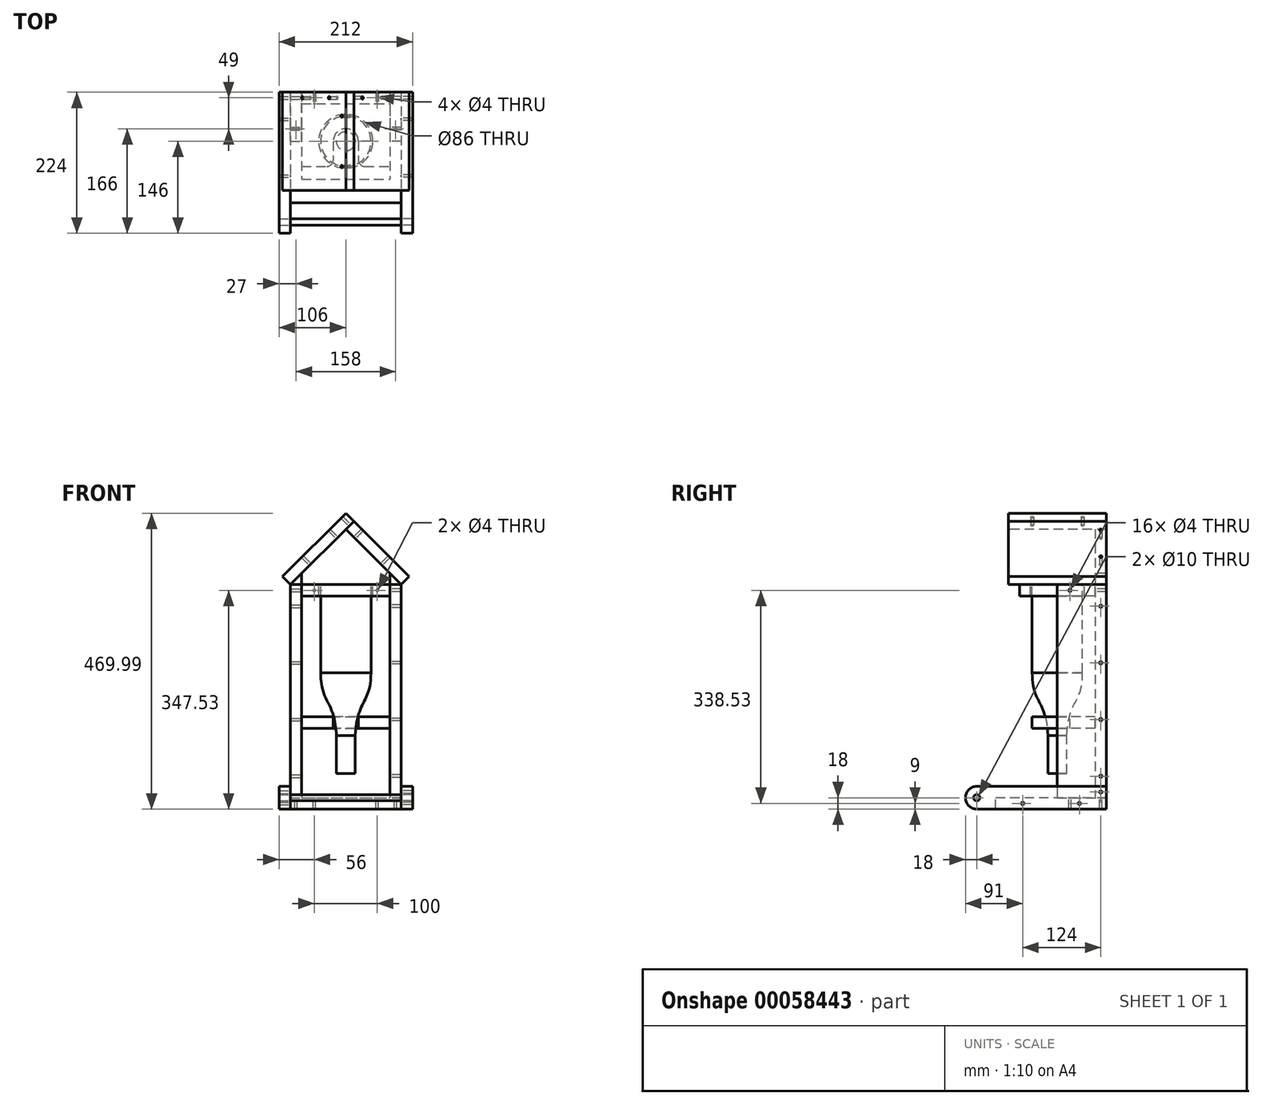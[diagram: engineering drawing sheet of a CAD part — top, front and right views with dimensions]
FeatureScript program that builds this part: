
annotation { "Feature Type Name" : "Feature", "Feature Type Description" : "" }
export const myFeature = defineFeature(function(context is Context, id is Id, definition is map)
    precondition{}
    {
        {
            assignVariable(context, id + "F0", {"name" : "Thickness", "anyValue" : 18});
        }
        {
            var Q0;
            Q0=qCreatedBy(makeId("Front.planeOp"),FACE);
            var sketch = newSketch(context, id + "F1", { "sketchPlane" : qUnion([Q0])});
            skLineSegment(sketch, "E0", {"start": v(0, 0) * mm, "end": v(40, 0) * mm});
            skLineSegment(sketch, "E1", {"start": v(40, 0) * mm, "end": v(40, -140) * mm});
            skLineSegment(sketch, "E2", {"start": v(15, -240) * mm, "end": v(15, -300) * mm});
            skLineSegment(sketch, "E3", {"start": v(0, 0) * mm, "end": v(0, -300) * mm});
            skLineSegment(sketch, "E4", {"start": v(15, -300) * mm, "end": v(0, -300) * mm});
            skFitSpline(sketch, "E5", {"points": [v(40, -140) * mm, v(15, -240) * mm], "startDerivative": vector(-0.64, -151.3) * mm, "endDerivative": vector(-7.4, -174.03) * mm});
            skSolve(sketch);
        }
        {
            var Q0;
            Q0=makeQuery(id+"F1.imprint","IMPRINT",FACE,{"disambiguationData":[TD([[makeQuery(id+"F1.imprint","IMPRINT",EDGE,{"derivedFrom":sQuery(id+"F1.wireOp",EDGE,"E0")}),-1.0]])]});
            var Q1;
            Q1=sQuery(id+"F1.wireOp",EDGE,"E3");
            revolve(context, id + "F2", {"entities" : qUnion([Q0]), "axis" : qUnion([Q1]), "revolveType" : RevolveType.FULL});
        }
        {
            var Q0;
            Q0=qCreatedBy(makeId("Front.planeOp"),FACE);
            cPlane(context, id + "F3", {"entities" : qUnion([Q0]), "cplaneType" : CPlaneType.OFFSET, "offset" : 60 * mm, "oppositeDirection" : true, "width" : 150 * mm, "height" : 150 * mm});
        }
        {
            var Q0;
            Q0=qCreatedBy(id+"F3.planeOp",FACE);
            var sketch = newSketch(context, id + "F4", { "sketchPlane" : qUnion([Q0])});
            skLineSegment(sketch, "E6.bottom", {"start": v(-70, 18) * mm, "end": v(70, 18) * mm, "construction": true});
            skLineSegment(sketch, "E6.top", {"start": v(-70, -338.53) * mm, "end": v(70, -338.53) * mm});
            skLineSegment(sketch, "E6.left", {"start": v(-70, 18) * mm, "end": v(-70, -338.53) * mm});
            skLineSegment(sketch, "E6.right", {"start": v(70, 18) * mm, "end": v(70, -338.53) * mm});
            skLineSegment(sketch, "E7.bottom", {"start": v(70, 0) * mm, "end": v(88, 0) * mm, "construction": true});
            skLineSegment(sketch, "E7.top", {"start": v(70, -338.53) * mm, "end": v(88, -338.53) * mm, "construction": true});
            skLineSegment(sketch, "E7.left", {"start": v(70, 0) * mm, "end": v(70, -338.53) * mm});
            skLineSegment(sketch, "E7.right", {"start": v(88, 0) * mm, "end": v(88, -338.53) * mm, "construction": true});
            skLineSegment(sketch, "E8", {"start": v(-40, -140) * mm, "end": v(-40, 0) * mm, "construction": true});
            skLineSegment(sketch, "E9", {"start": v(0, 18) * mm, "end": v(0, -338.53) * mm, "construction": true});
            skLineSegment(sketch, "E10.MirrorCS", {"start": v(-70, -338.53) * mm, "end": v(-88, -338.53) * mm, "construction": true});
            skLineSegment(sketch, "E11.MirrorCS", {"start": v(-88, 0) * mm, "end": v(-88, -338.53) * mm, "construction": true});
            skLineSegment(sketch, "E12.MirrorCS", {"start": v(-70, 0) * mm, "end": v(-88, 0) * mm, "construction": true});
            skLineSegment(sketch, "E13", {"start": v(-70, 18) * mm, "end": v(0, 88) * mm});
            skLineSegment(sketch, "E14", {"start": v(0, 88) * mm, "end": v(70, 18) * mm});
            skLineSegment(sketch, "E15", {"start": v(70, -9) * mm, "end": v(-70, -9) * mm, "construction": true});
            skCircle(sketch, "E16", {"center": v(50, -9) * mm, "radius": 2 * mm});
            skCircle(sketch, "E17.MirrorC", {"center": v(-50, -9) * mm, "radius": 2 * mm});
            skSolve(sketch);
        }
        {
            var Q0;
            Q0 = qSketchRegion(id + "F4", true);
            extrude(context, id + "F5", {"entities" : qUnion([Q0]), "oppositeDirection" : true, "depth" : (getVariable(context, 'Thickness')) * mm});
        }
        {
            var Q0;
            Q0=makeQuery(id+"F5.opExtrude","SWEPT_FACE",FACE,{"disambiguationData":[OSD([sQuery(id+"F4.wireOp",EDGE,"E6.right"),sQuery(id+"F4.wireOp",EDGE,"E7.left")])]});
            var sketch = newSketch(context, id + "F6", { "sketchPlane" : qUnion([Q0])});
            skLineSegment(sketch, "E18.bottom", {"start": v(78, 0) * mm, "end": v(0, 0) * mm});
            skLineSegment(sketch, "E18.top", {"start": v(78, -338.53) * mm, "end": v(0, -338.53) * mm});
            skLineSegment(sketch, "E18.left", {"start": v(78, 0) * mm, "end": v(78, -338.53) * mm});
            skLineSegment(sketch, "E18.right", {"start": v(0, 0) * mm, "end": v(0, -338.53) * mm});
            skLineSegment(sketch, "E19", {"start": v(69, 0) * mm, "end": v(69, -338.53) * mm, "construction": true});
            skCircle(sketch, "E20", {"center": v(69, -34.26) * mm, "radius": 2 * mm});
            skCircle(sketch, "E21.0.1.0", {"center": v(69, -124.26) * mm, "radius": 2 * mm});
            skCircle(sketch, "E21.0.2.0", {"center": v(69, -214.26) * mm, "radius": 2 * mm});
            skCircle(sketch, "E21.0.3.0", {"center": v(69, -304.26) * mm, "radius": 2 * mm});
            skLineSegment(sketch, "E21.direction1", {"start": v(69, -34.26) * mm, "end": v(84, -34.26) * mm, "construction": true});
            skLineSegment(sketch, "E21.direction2", {"start": v(69, -34.26) * mm, "end": v(69, -124.26) * mm, "construction": true});
            skLineSegment(sketch, "E22", {"start": v(60, -169.26) * mm, "end": v(78, -169.26) * mm, "construction": true});
            skLineSegment(sketch, "E23", {"start": v(78, -9) * mm, "end": v(0, -9) * mm, "construction": true});
            skCircle(sketch, "E24", {"center": v(20, -9) * mm, "radius": 2 * mm});
            skSolve(sketch);
        }
        {
            var Q0;
            Q0 = qSketchRegion(id + "F6", true);
            extrude(context, id + "F7", {"entities" : qUnion([Q0]), "depth" : (getVariable(context, 'Thickness')) * mm});
        }
        {
            var Q0;
            Q0=makeQuery(id+"F5.opExtrude","SWEPT_FACE",FACE,{"disambiguationData":[OSD([sQuery(id+"F4.wireOp",EDGE,"E6.left")])]});
            var sketch = newSketch(context, id + "F8", { "sketchPlane" : qUnion([Q0])});
            skLineSegment(sketch, "E25.bottom", {"start": v(0, 0) * mm, "end": v(-78, 0) * mm});
            skLineSegment(sketch, "E25.top", {"start": v(0, -338.53) * mm, "end": v(-78, -338.53) * mm});
            skLineSegment(sketch, "E25.left", {"start": v(0, 0) * mm, "end": v(0, -338.53) * mm});
            skLineSegment(sketch, "E25.right", {"start": v(-78, 0) * mm, "end": v(-78, -338.53) * mm});
            skCircle(sketch, "E26.0", {"center": v(-69, -34.26) * mm, "radius": 2 * mm});
            skCircle(sketch, "E27.0", {"center": v(-69, -124.26) * mm, "radius": 2 * mm});
            skCircle(sketch, "E28.0", {"center": v(-69, -214.26) * mm, "radius": 2 * mm});
            skCircle(sketch, "E29.0", {"center": v(-69, -304.26) * mm, "radius": 2 * mm});
            skCircle(sketch, "E30.0", {"center": v(-20, -9) * mm, "radius": 2 * mm});
            skSolve(sketch);
        }
        {
            var Q0;
            Q0 = qSketchRegion(id + "F8", true);
            extrude(context, id + "F9", {"entities" : qUnion([Q0]), "depth" : (getVariable(context, 'Thickness')) * mm});
        }
        {
            var Q0;
            Q0=makeQuery(id+"F5.opExtrude","SWEPT_FACE",FACE,{"disambiguationData":[OSD([sQuery(id+"F4.wireOp",EDGE,"E14")])]});
            var sketch = newSketch(context, id + "F10", { "sketchPlane" : qUnion([Q0])});
            skLineSegment(sketch, "E31.bottom", {"start": v(78, 62.23) * mm, "end": v(-78, 62.23) * mm});
            skLineSegment(sketch, "E31.top", {"start": v(78, -62.23) * mm, "end": v(-78, -62.23) * mm});
            skLineSegment(sketch, "E31.left", {"start": v(78, 62.23) * mm, "end": v(78, -62.23) * mm});
            skLineSegment(sketch, "E31.right", {"start": v(-78, 62.23) * mm, "end": v(-78, -62.23) * mm});
            skLineSegment(sketch, "E32", {"start": v(69, 62.23) * mm, "end": v(69, -36.77) * mm, "construction": true});
            skCircle(sketch, "E33", {"center": v(69, 42.73) * mm, "radius": 2 * mm});
            skCircle(sketch, "E34", {"center": v(69, -17.27) * mm, "radius": 2 * mm});
            skLineSegment(sketch, "E35", {"start": v(60, 12.73) * mm, "end": v(78, 12.73) * mm, "construction": true});
            skSolve(sketch);
        }
        {
            var Q0;
            Q0 = qSketchRegion(id + "F10", true);
            extrude(context, id + "F11", {"entities" : qUnion([Q0]), "depth" : (getVariable(context, 'Thickness')) * mm});
        }
        {
            var Q0;
            Q0=makeQuery(id+"F5.opExtrude","SWEPT_FACE",FACE,{"disambiguationData":[OSD([sQuery(id+"F4.wireOp",EDGE,"E13")])]});
            var sketch = newSketch(context, id + "F12", { "sketchPlane" : qUnion([Q0])});
            skLineSegment(sketch, "E36.bottom", {"start": v(78, 80.23) * mm, "end": v(-78, 80.23) * mm});
            skLineSegment(sketch, "E36.top", {"start": v(78, -62.23) * mm, "end": v(-78, -62.23) * mm});
            skLineSegment(sketch, "E36.left", {"start": v(78, 80.23) * mm, "end": v(78, -62.23) * mm});
            skLineSegment(sketch, "E36.right", {"start": v(-78, 80.23) * mm, "end": v(-78, -62.23) * mm});
            skLineSegment(sketch, "E37", {"start": v(-69, 62.23) * mm, "end": v(-69, -36.77) * mm, "construction": true});
            skCircle(sketch, "E38", {"center": v(-69, 42.73) * mm, "radius": 2 * mm});
            skCircle(sketch, "E39", {"center": v(-69, -17.27) * mm, "radius": 2 * mm});
            skLineSegment(sketch, "E40", {"start": v(-78, 12.73) * mm, "end": v(-60, 12.73) * mm, "construction": true});
            skLineSegment(sketch, "E41", {"start": v(-78, 71.23) * mm, "end": v(78, 71.23) * mm, "construction": true});
            skCircle(sketch, "E42", {"center": v(-40, 71.23) * mm, "radius": 2 * mm});
            skCircle(sketch, "E43", {"center": v(40, 71.23) * mm, "radius": 2 * mm});
            skLineSegment(sketch, "E44", {"start": v(0, 80.23) * mm, "end": v(0, 62.23) * mm, "construction": true});
            skPoint(sketch, "E44.endSnap0", {"position": v(0, 71.23) * mm});
            skSolve(sketch);
        }
        {
            var Q0;
            Q0 = qSketchRegion(id + "F12", true);
            extrude(context, id + "F13", {"entities" : qUnion([Q0]), "depth" : (getVariable(context, 'Thickness')) * mm});
        }
        {
            var Q0;
            Q0=makeQuery(id+"F7.opExtrude","SWEPT_FACE",FACE,{"disambiguationData":[OSD([sQuery(id+"F6.wireOp",EDGE,"E18.bottom")])]});
            var sketch = newSketch(context, id + "F14", { "sketchPlane" : qUnion([Q0])});
            skLineSegment(sketch, "E45.bottom", {"start": v(-70, 60) * mm, "end": v(70, 60) * mm});
            skLineSegment(sketch, "E45.top", {"start": v(-70, -60) * mm, "end": v(70, -60) * mm});
            skLineSegment(sketch, "E45.left", {"start": v(-70, 60) * mm, "end": v(-70, -60) * mm});
            skLineSegment(sketch, "E45.right", {"start": v(70, 60) * mm, "end": v(70, -60) * mm});
            skCircle(sketch, "E46.0", {"center": v(0, 0) * mm, "radius": 43 * mm});
            skLineSegment(sketch, "E47", {"start": v(70, 0) * mm, "end": v(-70, 0) * mm, "construction": true});
            skSolve(sketch);
        }
        {
            var Q0;
            Q0 = qSketchRegion(id + "F14", true);
            extrude(context, id + "F15", {"entities" : qUnion([Q0]), "oppositeDirection" : true, "depth" : (getVariable(context, 'Thickness')) * mm});
        }
        {
            var Q0;
            Q0=makeQuery(id+"F15.opExtrude","CAP_FACE",FACE,{"disambiguationData":[OSD([sQuery(id+"F14.wireOp",EDGE,"E45.bottom"),sQuery(id+"F14.wireOp",EDGE,"E45.top"),sQuery(id+"F14.wireOp",EDGE,"E45.left"),sQuery(id+"F14.wireOp",EDGE,"E45.right"),sQuery(id+"F14.wireOp",EDGE,"E46.0")])],"isStart":true});
            cPlane(context, id + "F16", {"entities" : qUnion([Q0]), "cplaneType" : CPlaneType.OFFSET, "offset" : 210 * mm, "oppositeDirection" : true, "width" : 150 * mm, "height" : 150 * mm});
        }
        {
            var Q0;
            Q0=qCreatedBy(id+"F16.planeOp",FACE);
            var sketch = newSketch(context, id + "F17", { "sketchPlane" : qUnion([Q0])});
            skLineSegment(sketch, "E48.bottom", {"start": v(-70, 60) * mm, "end": v(70, 60) * mm});
            skLineSegment(sketch, "E48.top", {"start": v(-70, -40) * mm, "end": v(-30, -40) * mm});
            skLineSegment(sketch, "E48.left", {"start": v(-70, 60) * mm, "end": v(-70, -40) * mm});
            skLineSegment(sketch, "E48.right", {"start": v(70, 60) * mm, "end": v(70, -40) * mm});
            skArc(sketch, "E49.0", {"start": v(20, 0) * mm, "mid": v(0, 20) * mm, "end": v(-20, 0) * mm});
            skLineSegment(sketch, "E50", {"start": v(-20, 0) * mm, "end": v(-20, -30) * mm});
            skLineSegment(sketch, "E51", {"start": v(20, 0) * mm, "end": v(20, -30) * mm});
            skLineSegment(sketch, "E52.trimOffspring", {"start": v(30, -40) * mm, "end": v(70, -40) * mm});
            skPoint(sketch, "E53.visualSharp", {"position": v(-20, -40) * mm});
            skArc(sketch, "E53.filletArc", {"start": v(-30, -40) * mm, "mid": v(-22.93, -37.07) * mm, "end": v(-20, -30) * mm});
            skPoint(sketch, "E54.visualSharp", {"position": v(20, -40) * mm});
            skArc(sketch, "E54.filletArc", {"start": v(20, -30) * mm, "mid": v(22.93, -37.07) * mm, "end": v(30, -40) * mm});
            skSolve(sketch);
        }
        {
            var Q0;
            Q0 = qSketchRegion(id + "F17", true);
            extrude(context, id + "F18", {"entities" : qUnion([Q0]), "oppositeDirection" : true, "depth" : (getVariable(context, 'Thickness')) * mm});
        }
        {
            var Q0;
            Q0=makeQuery(id+"F5.opExtrude","SWEPT_FACE",FACE,{"disambiguationData":[OSD([sQuery(id+"F4.wireOp",EDGE,"E6.top")])]});
            var sketch = newSketch(context, id + "F19", { "sketchPlane" : qUnion([Q0])});
            skLineSegment(sketch, "E55.bottom", {"start": v(-88, -78) * mm, "end": v(88, -78) * mm});
            skLineSegment(sketch, "E55.top", {"start": v(-88, 98) * mm, "end": v(88, 98) * mm});
            skLineSegment(sketch, "E55.left", {"start": v(-88, -78) * mm, "end": v(-88, 98) * mm});
            skLineSegment(sketch, "E55.right", {"start": v(88, -78) * mm, "end": v(88, 98) * mm});
            skLineSegment(sketch, "E56", {"start": v(-79, 0) * mm, "end": v(-79, -78) * mm, "construction": true});
            skLineSegment(sketch, "E57", {"start": v(-88, -69) * mm, "end": v(88, -69) * mm, "construction": true});
            skCircle(sketch, "E58", {"center": v(-79, -20) * mm, "radius": 2 * mm});
            skCircle(sketch, "E59", {"center": v(-50, -69) * mm, "radius": 2 * mm});
            skCircle(sketch, "E60.MirrorC", {"center": v(79, -20) * mm, "radius": 2 * mm});
            skCircle(sketch, "E61.MirrorC", {"center": v(50, -69) * mm, "radius": 2 * mm});
            skSolve(sketch);
        }
        {
            var Q0;
            Q0 = qSketchRegion(id + "F19", true);
            extrude(context, id + "F20", {"entities" : qUnion([Q0]), "depth" : (getVariable(context, 'Thickness')) * mm});
        }
        {
            var Q0;
            Q0=makeQuery(id+"F20.opExtrude","SWEPT_FACE",FACE,{"disambiguationData":[OSD([sQuery(id+"F19.wireOp",EDGE,"E55.left")])]});
            var sketch = newSketch(context, id + "F21", { "sketchPlane" : qUnion([Q0])});
            skLineSegment(sketch, "E62.bottom", {"start": v(-78, -356.53) * mm, "end": v(128, -356.53) * mm});
            skLineSegment(sketch, "E62.top", {"start": v(-78, -320.53) * mm, "end": v(128, -320.53) * mm});
            skLineSegment(sketch, "E62.left", {"start": v(-78, -356.53) * mm, "end": v(-78, -320.53) * mm});
            skLineSegment(sketch, "E63", {"start": v(155.22, -338.53) * mm, "end": v(-78, -338.53) * mm, "construction": true});
            skCircle(sketch, "E64", {"center": v(128, -338.53) * mm, "radius": 5 * mm});
            skArc(sketch, "E65", {"start": v(128, -356.53) * mm, "mid": v(146, -338.53) * mm, "end": v(128, -320.53) * mm});
            skPoint(sketch, "E66.orphan", {"position": v(155.22, -320.53) * mm});
            skPoint(sketch, "E67.orphan", {"position": v(155.22, -356.53) * mm});
            skLineSegment(sketch, "E68", {"start": v(-78, -329.53) * mm, "end": v(0, -329.53) * mm, "construction": true});
            skCircle(sketch, "E69", {"center": v(-69, -329.53) * mm, "radius": 2 * mm});
            skLineSegment(sketch, "E70", {"start": v(-78, -347.53) * mm, "end": v(98, -347.53) * mm, "construction": true});
            skCircle(sketch, "E71", {"center": v(-35, -347.53) * mm, "radius": 2 * mm});
            skCircle(sketch, "E72", {"center": v(55, -347.53) * mm, "radius": 2 * mm});
            skLineSegment(sketch, "E73", {"start": v(10, -338.53) * mm, "end": v(10, -356.53) * mm, "construction": true});
            skSolve(sketch);
        }
        {
            var Q0;
            {var subQ0=sQuery(id+"F21.wireOp",EDGE,"E62.top");Q0=makeQuery(id+"F21.imprint","IMPRINT",FACE,{"disambiguationData":[TD([[makeQuery(id+"F21.imprint","IMPRINT",EDGE,{"derivedFrom":subQ0}),-1.0]])]});}
            var Q1;
            Q1=makeQuery(id+"F21.imprint","IMPRINT",FACE,{"disambiguationData":[TD([[makeQuery(id+"F21.imprint","IMPRINT",EDGE,{"derivedFrom":sQuery(id+"F21.wireOp",EDGE,"E71")}),-1.0]])]});
            extrude(context, id + "F22", {"entities" : qUnion([Q0, Q1]), "depth" : (getVariable(context, 'Thickness')) * mm});
        }
        {
            var Q0;
            Q0=makeQuery(id+"F22.opExtrude","SWEPT_BODY",BODY,{"disambiguationData":[OSD([sQuery(id+"F21.wireOp",EDGE,"E62.bottom"),sQuery(id+"F21.wireOp",EDGE,"E62.top"),sQuery(id+"F21.wireOp",EDGE,"E62.left"),sQuery(id+"F21.wireOp",EDGE,"E64"),sQuery(id+"F21.wireOp",EDGE,"E65"),sQuery(id+"F21.wireOp",EDGE,"E69"),sQuery(id+"F21.wireOp",EDGE,"E71"),sQuery(id+"F21.wireOp",EDGE,"E72")])]});
            var Q1;
            Q1=qCreatedBy(makeId("Right.planeOp"),FACE);
            mirror(context, id + "F23", {"entities" : qUnion([Q0]), "mirrorPlane" : qUnion([Q1])});
        }
        {
            var Q0;
            Q0=makeQuery(id+"F22.opExtrude","CAP_FACE",FACE,{"disambiguationData":[OSD([sQuery(id+"F21.wireOp",EDGE,"E62.bottom"),sQuery(id+"F21.wireOp",EDGE,"E62.top"),sQuery(id+"F21.wireOp",EDGE,"E62.left"),sQuery(id+"F21.wireOp",EDGE,"E64"),sQuery(id+"F21.wireOp",EDGE,"E65"),sQuery(id+"F21.wireOp",EDGE,"E69"),sQuery(id+"F21.wireOp",EDGE,"E71"),sQuery(id+"F21.wireOp",EDGE,"E72")])],"isStart":false});
            var sketch = newSketch(context, id + "F24", { "sketchPlane" : qUnion([Q0])});
            skCircle(sketch, "E74.0", {"center": v(128, -338.53) * mm, "radius": 5 * mm});
            skSolve(sketch);
        }
        {
            var Q0;
            Q0 = qSketchRegion(id + "F24", true);
            var Q1;
            Q1=makeQuery(id+"F23.opPattern","COPY",FACE,{"derivedFrom":makeQuery(id+"F22.opExtrude","CAP_FACE",FACE,{"disambiguationData":[OSD([sQuery(id+"F21.wireOp",EDGE,"E62.bottom"),sQuery(id+"F21.wireOp",EDGE,"E62.top"),sQuery(id+"F21.wireOp",EDGE,"E62.left"),sQuery(id+"F21.wireOp",EDGE,"E64"),sQuery(id+"F21.wireOp",EDGE,"E65"),sQuery(id+"F21.wireOp",EDGE,"E69"),sQuery(id+"F21.wireOp",EDGE,"E71"),sQuery(id+"F21.wireOp",EDGE,"E72")])],"isStart":false}),"instanceName":"1"});
            extrude(context, id + "F25", {"entities" : qUnion([Q0]), "endBound" : BoundingType.UP_TO_SURFACE, "oppositeDirection" : true, "endBoundEntityFace" : qUnion([Q1]), "depth" : 25 * mm});
        }
    });
